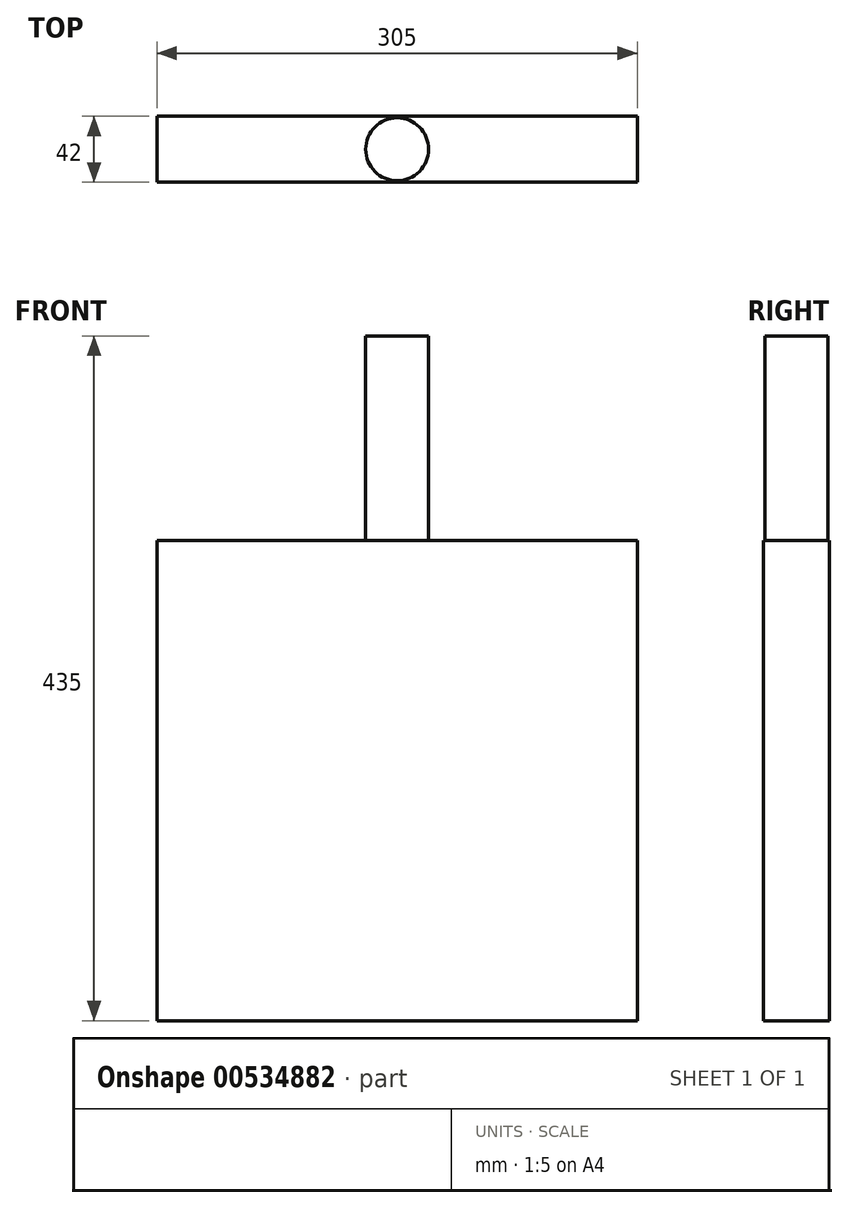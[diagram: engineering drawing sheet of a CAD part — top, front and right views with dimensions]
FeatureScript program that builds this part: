
annotation { "Feature Type Name" : "Feature", "Feature Type Description" : "" }
export const myFeature = defineFeature(function(context is Context, id is Id, definition is map)
    precondition{}
    {
        {
            var Q0;
            Q0=qCreatedBy(makeId("Front.planeOp"),FACE);
            var sketch = newSketch(context, id + "F0", { "sketchPlane" : qUnion([Q0])});
            skLineSegment(sketch, "E0.bottom", {"start": v(152.5, 152.5) * mm, "end": v(-152.5, 152.5) * mm});
            skLineSegment(sketch, "E0.top", {"start": v(152.5, -152.5) * mm, "end": v(-152.5, -152.5) * mm});
            skLineSegment(sketch, "E0.left", {"start": v(152.5, 152.5) * mm, "end": v(152.5, -152.5) * mm});
            skLineSegment(sketch, "E0.right", {"start": v(-152.5, 152.5) * mm, "end": v(-152.5, -152.5) * mm});
            skPoint(sketch, "E0.middle", {"position": v(0, 0) * mm});
            skSolve(sketch);
        }
        {
            var Q0;
            Q0 = qSketchRegion(id + "F0", true);
            extrude(context, id + "F1", {"entities" : qUnion([Q0]), "endBound" : BoundingType.SYMMETRIC, "depth" : 42 * mm, "offsetDistance" : 25 * mm});
        }
        {
            var Q0;
            Q0=makeQuery(id+"F1.opExtrude","SWEPT_FACE",FACE,{"disambiguationData":[OSD([sQuery(id+"F0.wireOp",EDGE,"E0.bottom")])]});
            var sketch = newSketch(context, id + "F2", { "sketchPlane" : qUnion([Q0])});
            skCircle(sketch, "E1", {"center": v(0, 0) * mm, "radius": 20 * mm});
            skSolve(sketch);
        }
        {
            var Q0;
            Q0=makeQuery(id+"F2.imprint","IMPRINT",FACE,{"disambiguationData":[TD([[makeQuery(id+"F2.imprint","IMPRINT",EDGE,{"derivedFrom":sQuery(id+"F2.wireOp",EDGE,"E1")}),1.0]])]});
            extrude(context, id + "F3", {"entities" : qUnion([Q0]), "operationType" : NewBodyOperationType.ADD, "depth" : 130 * mm, "offsetDistance" : 25 * mm});
        }
    });
